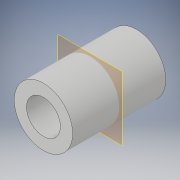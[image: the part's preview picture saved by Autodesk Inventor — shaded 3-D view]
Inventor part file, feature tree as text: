
AUTODESK INVENTOR PART (.ipt)
format: ipt  version: 2018 (Build 220112000, 112)  size: 113,664 bytes
history: native  units: in
note: dims shown in document units (in); Inventor stores cm internally (conversion verified against a paired STEP export)
features: extrude x3, sketch x3, plane x1
ambient origin geometry x8: Origin, YZ Plane, XZ Plane, XY Plane, X Axis, Y Axis, Z Axis, Center Point
bodies: Solid1 (feature_tree)
feature tree (7):
  extrude  "Extrusion1"  Depth=1.0781in
  plane  "Work Plane1"
  extrude  "Extrusion2"  Depth=0.5in TaperAngle=0.0deg
  extrude  "Extrusion3"  Depth=0.5in TaperAngle=0.0deg
  sketch  "Sketch1"  dims[d0=0.625in d1=1.0781in]
  sketch  "Sketch3"  dims[d2=1.7188in d3=0.0in d4=0.5in d5=0.0in]
  sketch  "Sketch5"  dims[d6=0.25in d7=0.5in d8=0.0in]
